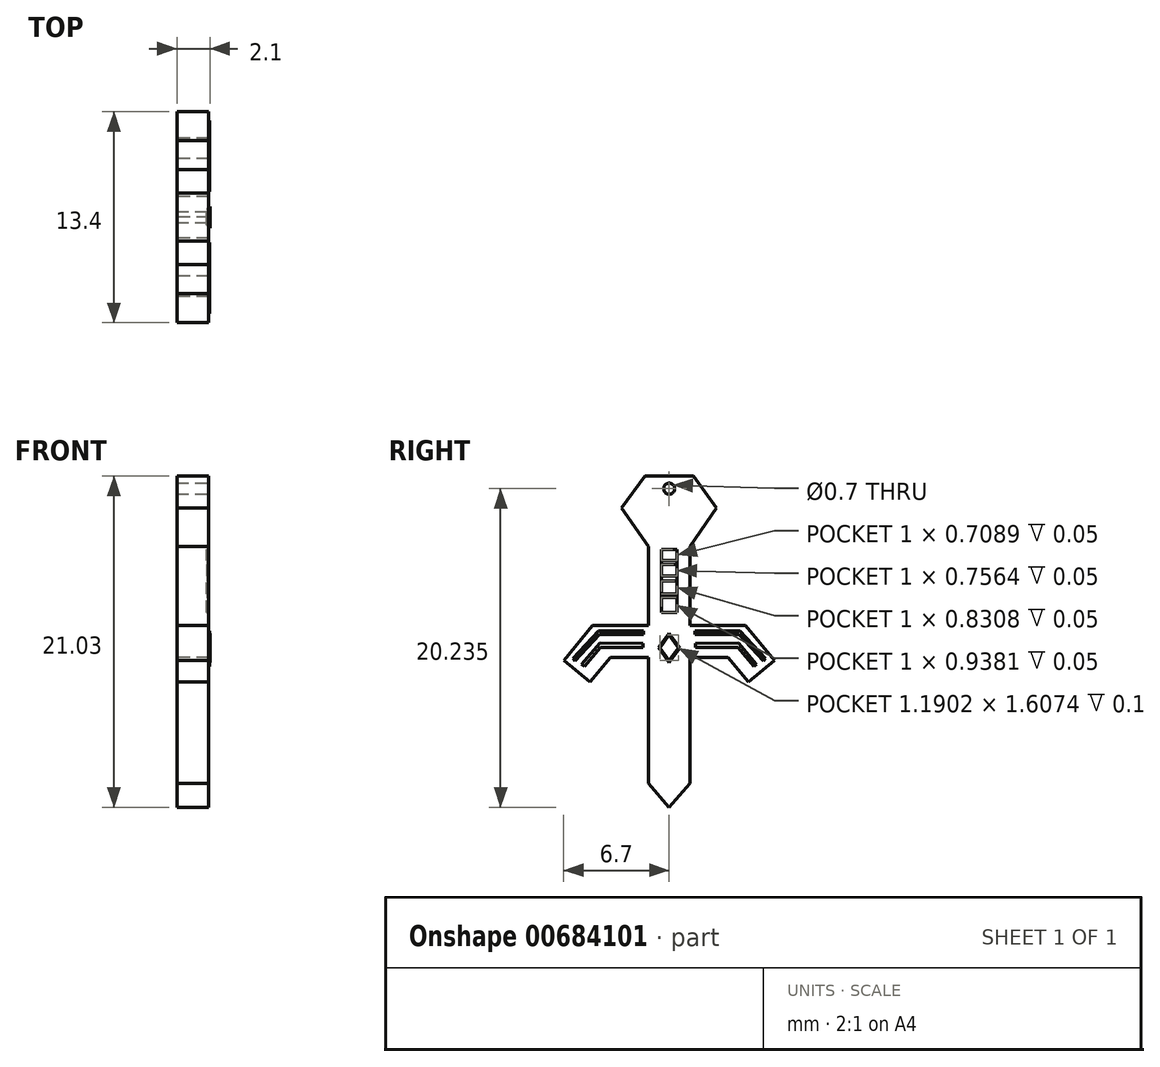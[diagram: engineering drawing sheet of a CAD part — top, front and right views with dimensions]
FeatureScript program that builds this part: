
annotation { "Feature Type Name" : "Feature", "Feature Type Description" : "" }
export const myFeature = defineFeature(function(context is Context, id is Id, definition is map)
    precondition{}
    {
        {
            var Q0;
            Q0=qCreatedBy(makeId("Right.planeOp"),FACE);
            var sketch = newSketch(context, id + "F0", { "sketchPlane" : qUnion([Q0])});
            skLineSegment(sketch, "E0", {"start": v(-2.47, 22.84) * mm, "end": v(1.53, 22.84) * mm});
            skLineSegment(sketch, "E1", {"start": v(1.53, 22.84) * mm, "end": v(3.02, 20.83) * mm});
            skLineSegment(sketch, "E2", {"start": v(3.02, 20.83) * mm, "end": v(1.31, 18.36) * mm});
            skLineSegment(sketch, "E3.MirrorCS", {"start": v(-1.53, 22.84) * mm, "end": v(-3.02, 20.83) * mm});
            skLineSegment(sketch, "E4.MirrorCS", {"start": v(-3.02, 20.83) * mm, "end": v(-1.31, 18.36) * mm});
            skLineSegment(sketch, "E5", {"start": v(-1.31, 18.36) * mm, "end": v(-1.31, 13.36) * mm});
            skLineSegment(sketch, "E6.MirrorCS", {"start": v(1.31, 18.36) * mm, "end": v(1.31, 13.36) * mm});
            skLineSegment(sketch, "E7", {"start": v(-1.31, 13.36) * mm, "end": v(-4.86, 13.36) * mm});
            skLineSegment(sketch, "E8", {"start": v(-4.86, 13.36) * mm, "end": v(-6.7, 11.15) * mm});
            skLineSegment(sketch, "E9", {"start": v(-6.7, 11.15) * mm, "end": v(-5.03, 9.76) * mm});
            skLineSegment(sketch, "E10", {"start": v(-5.03, 9.76) * mm, "end": v(-3.73, 11.32) * mm});
            skLineSegment(sketch, "E11", {"start": v(-3.73, 11.32) * mm, "end": v(-1.31, 11.32) * mm});
            skLineSegment(sketch, "E12.MirrorCS", {"start": v(3.73, 11.32) * mm, "end": v(1.31, 11.32) * mm});
            skLineSegment(sketch, "E13.MirrorCS", {"start": v(1.31, 13.36) * mm, "end": v(4.86, 13.36) * mm});
            skLineSegment(sketch, "E14.MirrorCS", {"start": v(4.86, 13.36) * mm, "end": v(6.7, 11.15) * mm});
            skLineSegment(sketch, "E15.MirrorCS", {"start": v(6.7, 11.15) * mm, "end": v(5.03, 9.76) * mm});
            skLineSegment(sketch, "E16.MirrorCS", {"start": v(5.03, 9.76) * mm, "end": v(3.73, 11.32) * mm});
            skLineSegment(sketch, "E17", {"start": v(-1.31, 11.32) * mm, "end": v(-1.31, 3.32) * mm});
            skLineSegment(sketch, "E18", {"start": v(-1.31, 3.32) * mm, "end": v(0, 1.81) * mm});
            skLineSegment(sketch, "E19.MirrorCS", {"start": v(1.31, 11.32) * mm, "end": v(1.31, 3.32) * mm});
            skLineSegment(sketch, "E20.MirrorCS", {"start": v(1.31, 3.32) * mm, "end": v(0, 1.81) * mm});
            skSolve(sketch);
        }
        {
            var Q0;
            Q0 = qSketchRegion(id + "F0", true);
            extrude(context, id + "F1", {"entities" : qUnion([Q0]), "depth" : 2 * mm, "offsetDistance" : 25 * mm});
        }
        {
            var Q0;
            Q0=makeQuery(id+"F1.opExtrude","CAP_FACE",FACE,{"disambiguationData":[OSD([sQuery(id+"F0.wireOp",EDGE,"E0"),sQuery(id+"F0.wireOp",EDGE,"E1"),sQuery(id+"F0.wireOp",EDGE,"E2"),sQuery(id+"F0.wireOp",EDGE,"E3.MirrorCS"),sQuery(id+"F0.wireOp",EDGE,"E4.MirrorCS"),sQuery(id+"F0.wireOp",EDGE,"E5"),sQuery(id+"F0.wireOp",EDGE,"E6.MirrorCS"),sQuery(id+"F0.wireOp",EDGE,"E7"),sQuery(id+"F0.wireOp",EDGE,"E8"),sQuery(id+"F0.wireOp",EDGE,"E9"),sQuery(id+"F0.wireOp",EDGE,"E10"),sQuery(id+"F0.wireOp",EDGE,"E11"),sQuery(id+"F0.wireOp",EDGE,"E12.MirrorCS"),sQuery(id+"F0.wireOp",EDGE,"E13.MirrorCS"),sQuery(id+"F0.wireOp",EDGE,"E14.MirrorCS"),sQuery(id+"F0.wireOp",EDGE,"E15.MirrorCS"),sQuery(id+"F0.wireOp",EDGE,"E16.MirrorCS"),sQuery(id+"F0.wireOp",EDGE,"E17"),sQuery(id+"F0.wireOp",EDGE,"E18"),sQuery(id+"F0.wireOp",EDGE,"E19.MirrorCS"),sQuery(id+"F0.wireOp",EDGE,"E20.MirrorCS")])],"isStart":false});
            var sketch = newSketch(context, id + "F2", { "sketchPlane" : qUnion([Q0])});
            skCircle(sketch, "E21", {"center": v(0, 22.05) * mm, "radius": 0.35 * mm});
            skSolve(sketch);
        }
        {
            var Q0;
            Q0 = qSketchRegion(id + "F2", true);
            extrude(context, id + "F3", {"entities" : qUnion([Q0]), "operationType" : NewBodyOperationType.REMOVE, "oppositeDirection" : true, "depth" : 25 * mm, "offsetDistance" : 25 * mm});
        }
        {
            var Q0;
            Q0=makeQuery(id+"F1.opExtrude","CAP_FACE",FACE,{"disambiguationData":[OSD([sQuery(id+"F0.wireOp",EDGE,"E0"),sQuery(id+"F0.wireOp",EDGE,"E1"),sQuery(id+"F0.wireOp",EDGE,"E2"),sQuery(id+"F0.wireOp",EDGE,"E3.MirrorCS"),sQuery(id+"F0.wireOp",EDGE,"E4.MirrorCS"),sQuery(id+"F0.wireOp",EDGE,"E5"),sQuery(id+"F0.wireOp",EDGE,"E6.MirrorCS"),sQuery(id+"F0.wireOp",EDGE,"E7"),sQuery(id+"F0.wireOp",EDGE,"E8"),sQuery(id+"F0.wireOp",EDGE,"E9"),sQuery(id+"F0.wireOp",EDGE,"E10"),sQuery(id+"F0.wireOp",EDGE,"E11"),sQuery(id+"F0.wireOp",EDGE,"E12.MirrorCS"),sQuery(id+"F0.wireOp",EDGE,"E13.MirrorCS"),sQuery(id+"F0.wireOp",EDGE,"E14.MirrorCS"),sQuery(id+"F0.wireOp",EDGE,"E15.MirrorCS"),sQuery(id+"F0.wireOp",EDGE,"E16.MirrorCS"),sQuery(id+"F0.wireOp",EDGE,"E17"),sQuery(id+"F0.wireOp",EDGE,"E18"),sQuery(id+"F0.wireOp",EDGE,"E19.MirrorCS"),sQuery(id+"F0.wireOp",EDGE,"E20.MirrorCS")])],"isStart":false});
            var sketch = newSketch(context, id + "F4", { "sketchPlane" : qUnion([Q0])});
            skLineSegment(sketch, "E22", {"start": v(-0.5, 18.18) * mm, "end": v(0.5, 18.18) * mm});
            skLineSegment(sketch, "E23", {"start": v(0.5, 18.18) * mm, "end": v(0.5, 14.18) * mm});
            skLineSegment(sketch, "E24", {"start": v(0.5, 14.18) * mm, "end": v(-0.5, 14.18) * mm});
            skLineSegment(sketch, "E25", {"start": v(-0.5, 14.18) * mm, "end": v(-0.5, 18.18) * mm});
            skLineSegment(sketch, "E26", {"start": v(-0.5, 17.15) * mm, "end": v(0.5, 17.15) * mm});
            skLineSegment(sketch, "E27", {"start": v(-0.5, 15.86) * mm, "end": v(0.5, 15.86) * mm});
            skPoint(sketch, "E27.startSnap0", {"position": v(-1.31, 15.86) * mm});
            skLineSegment(sketch, "E28", {"start": v(-0.5, 15.01) * mm, "end": v(0.5, 15.01) * mm});
            skSolve(sketch);
        }
        {
            var Q0;
            Q0 = qSketchRegion(id + "F4", true);
            extrude(context, id + "F5", {"entities" : qUnion([Q0]), "operationType" : NewBodyOperationType.REMOVE, "oppositeDirection" : true, "depth" : 0.1 * mm, "offsetDistance" : 25 * mm});
        }
        {
            var Q0;
            Q0=makeQuery(id+"F5.boolean.opBoolean","COPY",FACE,{"derivedFrom":makeQuery(id+"F5.opExtrude","CAP_FACE",FACE,{"disambiguationData":[OSD([sQuery(id+"F4.wireOp",EDGE,"E22"),sQuery(id+"F4.wireOp",EDGE,"E23"),sQuery(id+"F4.wireOp",EDGE,"E24"),sQuery(id+"F4.wireOp",EDGE,"E25")])],"isStart":false})});
            var sketch = newSketch(context, id + "F6", { "sketchPlane" : qUnion([Q0])});
            skLineSegment(sketch, "E29", {"start": v(-0.5, 15.12) * mm, "end": v(0.5, 15.12) * mm});
            skLineSegment(sketch, "E30", {"start": v(0.5, 15.12) * mm, "end": v(0.5, 15.35) * mm});
            skLineSegment(sketch, "E31", {"start": v(0.5, 15.35) * mm, "end": v(-0.5, 15.35) * mm});
            skLineSegment(sketch, "E32", {"start": v(-0.5, 16.18) * mm, "end": v(0.5, 16.18) * mm});
            skLineSegment(sketch, "E33", {"start": v(0.5, 16.18) * mm, "end": v(0.5, 16.49) * mm});
            skLineSegment(sketch, "E34", {"start": v(0.5, 16.49) * mm, "end": v(-0.5, 16.49) * mm});
            skLineSegment(sketch, "E35", {"start": v(-0.5, 17.47) * mm, "end": v(0.5, 17.47) * mm});
            skLineSegment(sketch, "E36", {"start": v(0.5, 17.47) * mm, "end": v(0.5, 17.24) * mm});
            skLineSegment(sketch, "E37", {"start": v(0.5, 17.24) * mm, "end": v(-0.5, 17.24) * mm});
            skSolve(sketch);
        }
        {
            var Q0;
            {var subQ0=sQuery(id+"F6.wireOp",EDGE,"E32");Q0=makeQuery(id+"F6.imprint","IMPRINT",FACE,{"disambiguationData":[TD([[makeQuery(id+"F6.imprint","IMPRINT",EDGE,{"derivedFrom":subQ0}),1.0]])]});}
            var Q1;
            {var subQ0=sQuery(id+"F6.wireOp",EDGE,"E29");Q1=makeQuery(id+"F6.imprint","IMPRINT",FACE,{"disambiguationData":[TD([[makeQuery(id+"F6.imprint","IMPRINT",EDGE,{"derivedFrom":subQ0}),1.0]])]});}
            var Q2;
            {var subQ0=sQuery(id+"F6.wireOp",EDGE,"E35");Q2=makeQuery(id+"F6.imprint","IMPRINT",FACE,{"disambiguationData":[TD([[makeQuery(id+"F6.imprint","IMPRINT",EDGE,{"derivedFrom":subQ0}),-1.0]])]});}
            extrude(context, id + "F7", {"entities" : qUnion([Q0, Q1, Q2]), "operationType" : NewBodyOperationType.ADD, "depth" : 0.05 * mm, "offsetDistance" : 25 * mm});
        }
        {
            var Q0;
            Q0=makeQuery(id+"F1.opExtrude","CAP_FACE",FACE,{"disambiguationData":[OSD([sQuery(id+"F0.wireOp",EDGE,"E0"),sQuery(id+"F0.wireOp",EDGE,"E1"),sQuery(id+"F0.wireOp",EDGE,"E2"),sQuery(id+"F0.wireOp",EDGE,"E3.MirrorCS"),sQuery(id+"F0.wireOp",EDGE,"E4.MirrorCS"),sQuery(id+"F0.wireOp",EDGE,"E5"),sQuery(id+"F0.wireOp",EDGE,"E6.MirrorCS"),sQuery(id+"F0.wireOp",EDGE,"E7"),sQuery(id+"F0.wireOp",EDGE,"E8"),sQuery(id+"F0.wireOp",EDGE,"E9"),sQuery(id+"F0.wireOp",EDGE,"E10"),sQuery(id+"F0.wireOp",EDGE,"E11"),sQuery(id+"F0.wireOp",EDGE,"E12.MirrorCS"),sQuery(id+"F0.wireOp",EDGE,"E13.MirrorCS"),sQuery(id+"F0.wireOp",EDGE,"E14.MirrorCS"),sQuery(id+"F0.wireOp",EDGE,"E15.MirrorCS"),sQuery(id+"F0.wireOp",EDGE,"E16.MirrorCS"),sQuery(id+"F0.wireOp",EDGE,"E17"),sQuery(id+"F0.wireOp",EDGE,"E18"),sQuery(id+"F0.wireOp",EDGE,"E19.MirrorCS"),sQuery(id+"F0.wireOp",EDGE,"E20.MirrorCS")])],"isStart":false});
            var sketch = newSketch(context, id + "F8", { "sketchPlane" : qUnion([Q0])});
            skLineSegment(sketch, "E38", {"start": v(0, 12.75) * mm, "end": v(-0.6, 11.94) * mm});
            skLineSegment(sketch, "E39", {"start": v(-0.6, 11.94) * mm, "end": v(0, 11.14) * mm});
            skLineSegment(sketch, "E40.MirrorCS", {"start": v(0, 12.75) * mm, "end": v(0.6, 11.94) * mm});
            skLineSegment(sketch, "E41.MirrorCS", {"start": v(0.6, 11.94) * mm, "end": v(0, 11.14) * mm});
            skLineSegment(sketch, "E42", {"start": v(0, 12.85) * mm, "end": v(0.67, 11.94) * mm});
            skLineSegment(sketch, "E43", {"start": v(0.67, 11.94) * mm, "end": v(0, 11.02) * mm});
            skLineSegment(sketch, "E44", {"start": v(0, 11.02) * mm, "end": v(-0.69, 11.95) * mm});
            skLineSegment(sketch, "E45", {"start": v(-0.69, 11.95) * mm, "end": v(0, 12.85) * mm});
            skSolve(sketch);
        }
        {
            var Q0;
            Q0 = qSketchRegion(id + "F8", true);
            extrude(context, id + "F9", {"entities" : qUnion([Q0]), "operationType" : NewBodyOperationType.ADD, "depth" : 0.1 * mm, "offsetDistance" : 25 * mm});
        }
        {
            var Q0;
            {var subQ0=sQuery(id+"F0.wireOp",EDGE,"E20.MirrorCS");var subQ1=sQuery(id+"F0.wireOp",EDGE,"E19.MirrorCS");var subQ2=sQuery(id+"F0.wireOp",EDGE,"E18");var subQ3=sQuery(id+"F0.wireOp",EDGE,"E17");var subQ4=sQuery(id+"F0.wireOp",EDGE,"E16.MirrorCS");var subQ5=sQuery(id+"F0.wireOp",EDGE,"E15.MirrorCS");var subQ6=sQuery(id+"F0.wireOp",EDGE,"E14.MirrorCS");var subQ7=sQuery(id+"F0.wireOp",EDGE,"E13.MirrorCS");var subQ8=sQuery(id+"F0.wireOp",EDGE,"E12.MirrorCS");var subQ9=sQuery(id+"F0.wireOp",EDGE,"E4.MirrorCS");var subQ10=sQuery(id+"F0.wireOp",EDGE,"E11");var subQ11=sQuery(id+"F0.wireOp",EDGE,"E10");var subQ12=sQuery(id+"F0.wireOp",EDGE,"E2");var subQ13=sQuery(id+"F0.wireOp",EDGE,"E1");var subQ14=sQuery(id+"F0.wireOp",EDGE,"E3.MirrorCS");var subQ15=sQuery(id+"F0.wireOp",EDGE,"E0");var subQ16=sQuery(id+"F0.wireOp",EDGE,"E9");var subQ17=sQuery(id+"F0.wireOp",EDGE,"E5");var subQ18=sQuery(id+"F0.wireOp",EDGE,"E6.MirrorCS");var subQ19=sQuery(id+"F0.wireOp",EDGE,"E7");var subQ20=sQuery(id+"F0.wireOp",EDGE,"E8");Q0=makeQuery(id+"F9.boolean.opBoolean","SPLIT",FACE,{"disambiguationData":[TD([makeQuery(id+"F1.opExtrude","SWEPT_FACE",FACE,{"disambiguationData":[OSD([subQ15])]})])],"derivedFrom":makeQuery(id+"F1.opExtrude","CAP_FACE",FACE,{"disambiguationData":[OSD([subQ15,subQ13,subQ12,subQ14,subQ9,subQ17,subQ18,subQ19,subQ20,subQ16,subQ11,subQ10,subQ8,subQ7,subQ6,subQ5,subQ4,subQ3,subQ2,subQ1,subQ0])],"isStart":false})});}
            var sketch = newSketch(context, id + "F10", { "sketchPlane" : qUnion([Q0])});
            skLineSegment(sketch, "E46", {"start": v(1.73, 12.95) * mm, "end": v(4.53, 12.95) * mm});
            skLineSegment(sketch, "E47", {"start": v(4.53, 12.95) * mm, "end": v(5.84, 11.41) * mm});
            skLineSegment(sketch, "E48", {"start": v(5.84, 11.41) * mm, "end": v(5.7, 11.29) * mm});
            skLineSegment(sketch, "E49", {"start": v(5.7, 11.29) * mm, "end": v(4.47, 12.72) * mm});
            skLineSegment(sketch, "E50", {"start": v(4.47, 12.72) * mm, "end": v(1.74, 12.72) * mm});
            skLineSegment(sketch, "E51", {"start": v(1.74, 12.72) * mm, "end": v(1.73, 12.95) * mm});
            skSolve(sketch);
        }
        {
            var Q0;
            Q0=makeQuery(id+"F10.imprint","IMPRINT",FACE,{"disambiguationData":[TD([[makeQuery(id+"F10.imprint","IMPRINT",EDGE,{"derivedFrom":sQuery(id+"F10.wireOp",EDGE,"E46")}),-1.0]])]});
            extrude(context, id + "F11", {"entities" : qUnion([Q0]), "operationType" : NewBodyOperationType.ADD, "oppositeDirection" : true, "depth" : 0.4 * mm, "offsetDistance" : 25 * mm});
        }
        {
            var Q0;
            {var subQ0=sQuery(id+"F0.wireOp",EDGE,"E20.MirrorCS");var subQ1=sQuery(id+"F0.wireOp",EDGE,"E19.MirrorCS");var subQ2=sQuery(id+"F0.wireOp",EDGE,"E18");var subQ3=sQuery(id+"F0.wireOp",EDGE,"E17");var subQ4=sQuery(id+"F0.wireOp",EDGE,"E16.MirrorCS");var subQ5=sQuery(id+"F0.wireOp",EDGE,"E15.MirrorCS");var subQ6=sQuery(id+"F0.wireOp",EDGE,"E14.MirrorCS");var subQ7=sQuery(id+"F0.wireOp",EDGE,"E13.MirrorCS");var subQ8=sQuery(id+"F0.wireOp",EDGE,"E12.MirrorCS");var subQ9=sQuery(id+"F0.wireOp",EDGE,"E4.MirrorCS");var subQ10=sQuery(id+"F0.wireOp",EDGE,"E11");var subQ11=sQuery(id+"F0.wireOp",EDGE,"E10");var subQ12=sQuery(id+"F0.wireOp",EDGE,"E2");var subQ13=sQuery(id+"F0.wireOp",EDGE,"E1");var subQ14=sQuery(id+"F0.wireOp",EDGE,"E3.MirrorCS");var subQ15=sQuery(id+"F0.wireOp",EDGE,"E0");var subQ16=sQuery(id+"F0.wireOp",EDGE,"E9");var subQ17=sQuery(id+"F0.wireOp",EDGE,"E5");var subQ18=sQuery(id+"F0.wireOp",EDGE,"E6.MirrorCS");var subQ19=sQuery(id+"F0.wireOp",EDGE,"E7");var subQ20=sQuery(id+"F0.wireOp",EDGE,"E8");Q0=makeQuery(id+"F9.boolean.opBoolean","SPLIT",FACE,{"disambiguationData":[TD([makeQuery(id+"F1.opExtrude","SWEPT_FACE",FACE,{"disambiguationData":[OSD([subQ15])]})])],"derivedFrom":makeQuery(id+"F1.opExtrude","CAP_FACE",FACE,{"disambiguationData":[OSD([subQ15,subQ13,subQ12,subQ14,subQ9,subQ17,subQ18,subQ19,subQ20,subQ16,subQ11,subQ10,subQ8,subQ7,subQ6,subQ5,subQ4,subQ3,subQ2,subQ1,subQ0])],"isStart":false})});}
            var sketch = newSketch(context, id + "F12", { "sketchPlane" : qUnion([Q0])});
            skLineSegment(sketch, "E52", {"start": v(1.7, 13.02) * mm, "end": v(1.7, 12.9) * mm});
            skLineSegment(sketch, "E53", {"start": v(1.7, 12.9) * mm, "end": v(4.5, 12.9) * mm});
            skLineSegment(sketch, "E54", {"start": v(4.5, 12.9) * mm, "end": v(5.75, 11.39) * mm});
            skLineSegment(sketch, "E55", {"start": v(5.75, 11.39) * mm, "end": v(5.83, 11.46) * mm});
            skLineSegment(sketch, "E56", {"start": v(5.83, 11.46) * mm, "end": v(4.55, 13.02) * mm});
            skLineSegment(sketch, "E57", {"start": v(4.55, 13.02) * mm, "end": v(1.7, 13.02) * mm});
            skLineSegment(sketch, "E58.MirrorCS", {"start": v(-1.7, 12.9) * mm, "end": v(-4.5, 12.9) * mm});
            skLineSegment(sketch, "E59.MirrorCS", {"start": v(-1.7, 13.02) * mm, "end": v(-1.7, 12.9) * mm});
            skLineSegment(sketch, "E60.MirrorCS", {"start": v(-4.55, 13.02) * mm, "end": v(-1.7, 13.02) * mm});
            skLineSegment(sketch, "E61.MirrorCS", {"start": v(-5.83, 11.46) * mm, "end": v(-4.55, 13.02) * mm});
            skLineSegment(sketch, "E62.MirrorCS", {"start": v(-4.5, 12.9) * mm, "end": v(-5.75, 11.39) * mm});
            skLineSegment(sketch, "E63.MirrorCS", {"start": v(-5.75, 11.39) * mm, "end": v(-5.83, 11.46) * mm});
            skSolve(sketch);
        }
        {
            var Q0;
            Q0=makeQuery(id+"F12.imprint","IMPRINT",FACE,{"disambiguationData":[TD([[makeQuery(id+"F12.imprint","IMPRINT",EDGE,{"derivedFrom":sQuery(id+"F12.wireOp",EDGE,"E52")}),1.0]])]});
            extrude(context, id + "F13", {"entities" : qUnion([Q0]), "operationType" : NewBodyOperationType.ADD, "oppositeDirection" : true, "depth" : 0.15 * mm, "offsetDistance" : 25 * mm});
        }
        {
            var Q0;
            {var subQ0=sQuery(id+"F0.wireOp",EDGE,"E20.MirrorCS");var subQ1=sQuery(id+"F0.wireOp",EDGE,"E19.MirrorCS");var subQ2=sQuery(id+"F0.wireOp",EDGE,"E18");var subQ3=sQuery(id+"F0.wireOp",EDGE,"E17");var subQ4=sQuery(id+"F0.wireOp",EDGE,"E16.MirrorCS");var subQ5=sQuery(id+"F0.wireOp",EDGE,"E15.MirrorCS");var subQ6=sQuery(id+"F0.wireOp",EDGE,"E14.MirrorCS");var subQ7=sQuery(id+"F0.wireOp",EDGE,"E13.MirrorCS");var subQ8=sQuery(id+"F0.wireOp",EDGE,"E12.MirrorCS");var subQ9=sQuery(id+"F0.wireOp",EDGE,"E4.MirrorCS");var subQ10=sQuery(id+"F0.wireOp",EDGE,"E11");var subQ11=sQuery(id+"F0.wireOp",EDGE,"E10");var subQ12=sQuery(id+"F0.wireOp",EDGE,"E2");var subQ13=sQuery(id+"F0.wireOp",EDGE,"E1");var subQ14=sQuery(id+"F0.wireOp",EDGE,"E3.MirrorCS");var subQ15=sQuery(id+"F0.wireOp",EDGE,"E0");var subQ16=sQuery(id+"F0.wireOp",EDGE,"E9");var subQ17=sQuery(id+"F0.wireOp",EDGE,"E5");var subQ18=sQuery(id+"F0.wireOp",EDGE,"E6.MirrorCS");var subQ19=sQuery(id+"F0.wireOp",EDGE,"E7");var subQ20=sQuery(id+"F0.wireOp",EDGE,"E8");Q0=makeQuery(id+"F9.boolean.opBoolean","SPLIT",FACE,{"disambiguationData":[TD([makeQuery(id+"F1.opExtrude","SWEPT_FACE",FACE,{"disambiguationData":[OSD([subQ15])]})])],"derivedFrom":makeQuery(id+"F1.opExtrude","CAP_FACE",FACE,{"disambiguationData":[OSD([subQ15,subQ13,subQ12,subQ14,subQ9,subQ17,subQ18,subQ19,subQ20,subQ16,subQ11,subQ10,subQ8,subQ7,subQ6,subQ5,subQ4,subQ3,subQ2,subQ1,subQ0])],"isStart":false})});}
            var sketch = newSketch(context, id + "F14", { "sketchPlane" : qUnion([Q0])});
            skLineSegment(sketch, "E64", {"start": v(-1.62, 12.8) * mm, "end": v(-1.62, 13) * mm});
            skLineSegment(sketch, "E65", {"start": v(-1.62, 13) * mm, "end": v(-4.5, 13) * mm});
            skLineSegment(sketch, "E66", {"start": v(-4.5, 13) * mm, "end": v(-6.13, 11.25) * mm});
            skLineSegment(sketch, "E67", {"start": v(-6.13, 11.25) * mm, "end": v(-5.98, 11.12) * mm});
            skLineSegment(sketch, "E68", {"start": v(-5.98, 11.12) * mm, "end": v(-4.43, 12.8) * mm});
            skLineSegment(sketch, "E69", {"start": v(-4.43, 12.8) * mm, "end": v(-1.62, 12.8) * mm});
            skLineSegment(sketch, "E70.MirrorCS", {"start": v(1.62, 12.8) * mm, "end": v(1.62, 13) * mm});
            skLineSegment(sketch, "E71.MirrorCS", {"start": v(1.62, 13) * mm, "end": v(4.5, 13) * mm});
            skLineSegment(sketch, "E72.MirrorCS", {"start": v(4.43, 12.8) * mm, "end": v(1.62, 12.8) * mm});
            skLineSegment(sketch, "E73.MirrorCS", {"start": v(5.98, 11.12) * mm, "end": v(4.43, 12.8) * mm});
            skLineSegment(sketch, "E74.MirrorCS", {"start": v(4.5, 13) * mm, "end": v(6.13, 11.25) * mm});
            skLineSegment(sketch, "E75.MirrorCS", {"start": v(6.13, 11.25) * mm, "end": v(5.98, 11.12) * mm});
            skSolve(sketch);
        }
        {
            var Q0;
            Q0=makeQuery(id+"F14.imprint","IMPRINT",FACE,{"disambiguationData":[TD([[makeQuery(id+"F14.imprint","IMPRINT",EDGE,{"derivedFrom":sQuery(id+"F14.wireOp",EDGE,"E64")}),1.0]])]});
            var Q1;
            Q1=makeQuery(id+"F14.imprint","IMPRINT",FACE,{"disambiguationData":[TD([[makeQuery(id+"F14.imprint","IMPRINT",EDGE,{"derivedFrom":sQuery(id+"F14.wireOp",EDGE,"E70.MirrorCS")}),-1.0]])]});
            extrude(context, id + "F15", {"entities" : qUnion([Q0, Q1]), "operationType" : NewBodyOperationType.ADD, "depth" : 0.08 * mm, "offsetDistance" : 25 * mm});
        }
        {
            var Q0;
            {var subQ0=sQuery(id+"F0.wireOp",EDGE,"E20.MirrorCS");var subQ1=sQuery(id+"F0.wireOp",EDGE,"E19.MirrorCS");var subQ2=sQuery(id+"F0.wireOp",EDGE,"E18");var subQ3=sQuery(id+"F0.wireOp",EDGE,"E17");var subQ4=sQuery(id+"F0.wireOp",EDGE,"E16.MirrorCS");var subQ5=sQuery(id+"F0.wireOp",EDGE,"E15.MirrorCS");var subQ6=sQuery(id+"F0.wireOp",EDGE,"E14.MirrorCS");var subQ7=sQuery(id+"F0.wireOp",EDGE,"E13.MirrorCS");var subQ8=sQuery(id+"F0.wireOp",EDGE,"E12.MirrorCS");var subQ9=sQuery(id+"F0.wireOp",EDGE,"E4.MirrorCS");var subQ10=sQuery(id+"F0.wireOp",EDGE,"E11");var subQ11=sQuery(id+"F0.wireOp",EDGE,"E10");var subQ12=sQuery(id+"F0.wireOp",EDGE,"E2");var subQ13=sQuery(id+"F0.wireOp",EDGE,"E1");var subQ14=sQuery(id+"F0.wireOp",EDGE,"E3.MirrorCS");var subQ15=sQuery(id+"F0.wireOp",EDGE,"E0");var subQ16=sQuery(id+"F0.wireOp",EDGE,"E9");var subQ17=sQuery(id+"F0.wireOp",EDGE,"E5");var subQ18=sQuery(id+"F0.wireOp",EDGE,"E6.MirrorCS");var subQ19=sQuery(id+"F0.wireOp",EDGE,"E7");var subQ20=sQuery(id+"F0.wireOp",EDGE,"E8");Q0=makeQuery(id+"F9.boolean.opBoolean","SPLIT",FACE,{"disambiguationData":[TD([makeQuery(id+"F1.opExtrude","SWEPT_FACE",FACE,{"disambiguationData":[OSD([subQ15])]})])],"derivedFrom":makeQuery(id+"F1.opExtrude","CAP_FACE",FACE,{"disambiguationData":[OSD([subQ15,subQ13,subQ12,subQ14,subQ9,subQ17,subQ18,subQ19,subQ20,subQ16,subQ11,subQ10,subQ8,subQ7,subQ6,subQ5,subQ4,subQ3,subQ2,subQ1,subQ0])],"isStart":false})});}
            var sketch = newSketch(context, id + "F16", { "sketchPlane" : qUnion([Q0])});
            skLineSegment(sketch, "E76", {"start": v(-1.67, 12.2) * mm, "end": v(-1.67, 11.97) * mm});
            skLineSegment(sketch, "E77", {"start": v(-1.67, 11.97) * mm, "end": v(-4.35, 11.97) * mm});
            skLineSegment(sketch, "E78", {"start": v(-4.35, 11.97) * mm, "end": v(-5.4, 10.74) * mm});
            skLineSegment(sketch, "E79", {"start": v(-5.4, 10.74) * mm, "end": v(-5.56, 10.88) * mm});
            skLineSegment(sketch, "E80", {"start": v(-5.56, 10.88) * mm, "end": v(-4.41, 12.24) * mm});
            skLineSegment(sketch, "E81", {"start": v(-4.41, 12.24) * mm, "end": v(-1.67, 12.2) * mm});
            skLineSegment(sketch, "E82.MirrorCS", {"start": v(1.67, 12.2) * mm, "end": v(1.67, 11.97) * mm});
            skLineSegment(sketch, "E83.MirrorCS", {"start": v(1.67, 11.97) * mm, "end": v(4.35, 11.97) * mm});
            skLineSegment(sketch, "E84.MirrorCS", {"start": v(4.41, 12.24) * mm, "end": v(1.67, 12.2) * mm});
            skLineSegment(sketch, "E85.MirrorCS", {"start": v(4.35, 11.97) * mm, "end": v(5.4, 10.74) * mm});
            skLineSegment(sketch, "E86.MirrorCS", {"start": v(5.56, 10.88) * mm, "end": v(4.41, 12.24) * mm});
            skLineSegment(sketch, "E87.MirrorCS", {"start": v(5.4, 10.74) * mm, "end": v(5.56, 10.88) * mm});
            skSolve(sketch);
        }
        {
            var Q0;
            Q0=makeQuery(id+"F16.imprint","IMPRINT",FACE,{"disambiguationData":[TD([[makeQuery(id+"F16.imprint","IMPRINT",EDGE,{"derivedFrom":sQuery(id+"F16.wireOp",EDGE,"E76")}),-1.0]])]});
            var Q1;
            Q1=makeQuery(id+"F16.imprint","IMPRINT",FACE,{"disambiguationData":[TD([[makeQuery(id+"F16.imprint","IMPRINT",EDGE,{"derivedFrom":sQuery(id+"F16.wireOp",EDGE,"E82.MirrorCS")}),1.0]])]});
            extrude(context, id + "F17", {"entities" : qUnion([Q0, Q1]), "operationType" : NewBodyOperationType.ADD, "depth" : 0.08 * mm, "offsetDistance" : 25 * mm});
        }
    });
